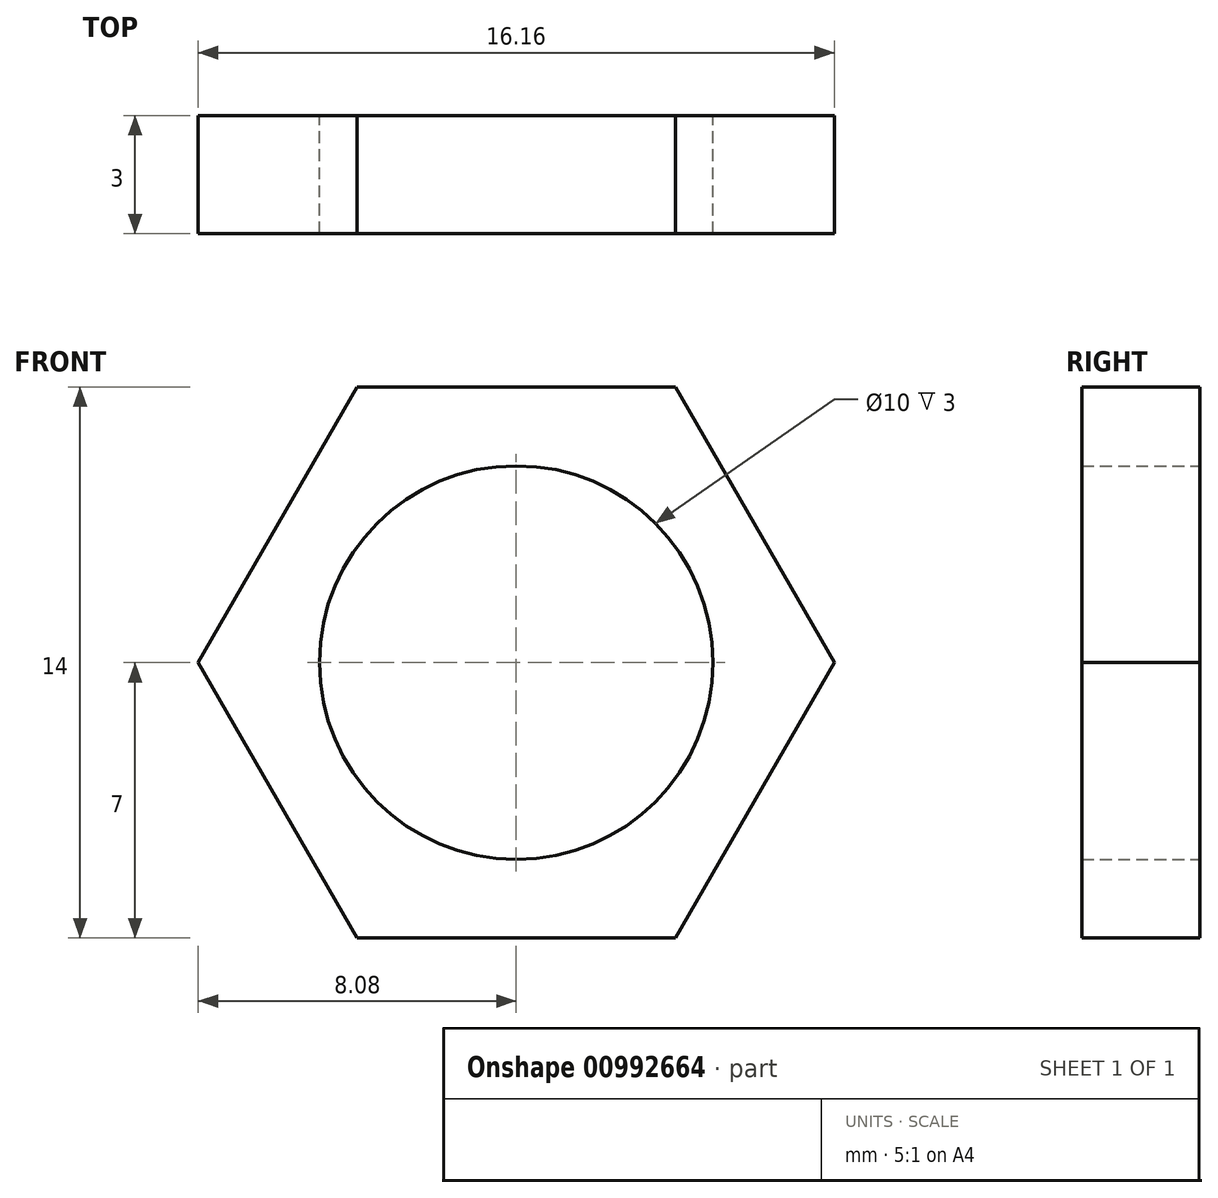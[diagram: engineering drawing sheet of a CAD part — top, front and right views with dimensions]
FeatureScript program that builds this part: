
annotation { "Feature Type Name" : "Feature", "Feature Type Description" : "" }
export const myFeature = defineFeature(function(context is Context, id is Id, definition is map)
    precondition{}
    {
        {
            var Q0;
            Q0=qCreatedBy(makeId("Front.planeOp"),FACE);
            var sketch = newSketch(context, id + "F0", { "sketchPlane" : qUnion([Q0])});
            skCircle(sketch, "E0.cCircle", {"center": v(0, 0) * mm, "radius": 7 * mm, "construction": true});
            skLineSegment(sketch, "E0.0", {"start": v(8.08, 0) * mm, "end": v(4.04, -7) * mm});
            skLineSegment(sketch, "E0.1", {"start": v(4.04, -7) * mm, "end": v(-4.04, -7) * mm});
            skLineSegment(sketch, "E0.2", {"start": v(-4.04, -7) * mm, "end": v(-8.08, 0) * mm});
            skLineSegment(sketch, "E0.3", {"start": v(-8.08, 0) * mm, "end": v(-4.04, 7) * mm});
            skLineSegment(sketch, "E0.4", {"start": v(-4.04, 7) * mm, "end": v(4.04, 7) * mm});
            skLineSegment(sketch, "E0.5", {"start": v(4.04, 7) * mm, "end": v(8.08, 0) * mm});
            skPoint(sketch, "E0.0.midPoint", {"position": v(6.06, -3.5) * mm});
            skCircle(sketch, "E1", {"center": v(0, 0) * mm, "radius": 5 * mm});
            skSolve(sketch);
        }
        {
            var Q0;
            Q0=makeQuery(id+"F0.imprint","IMPRINT",FACE,{"disambiguationData":[TD([[makeQuery(id+"F0.imprint","IMPRINT",EDGE,{"derivedFrom":sQuery(id+"F0.wireOp",EDGE,"E0.0")}),-1.0]])]});
            extrude(context, id + "F1", {"entities" : qUnion([Q0]), "depth" : 3 * mm, "offsetDistance" : 25 * mm});
        }
    });
